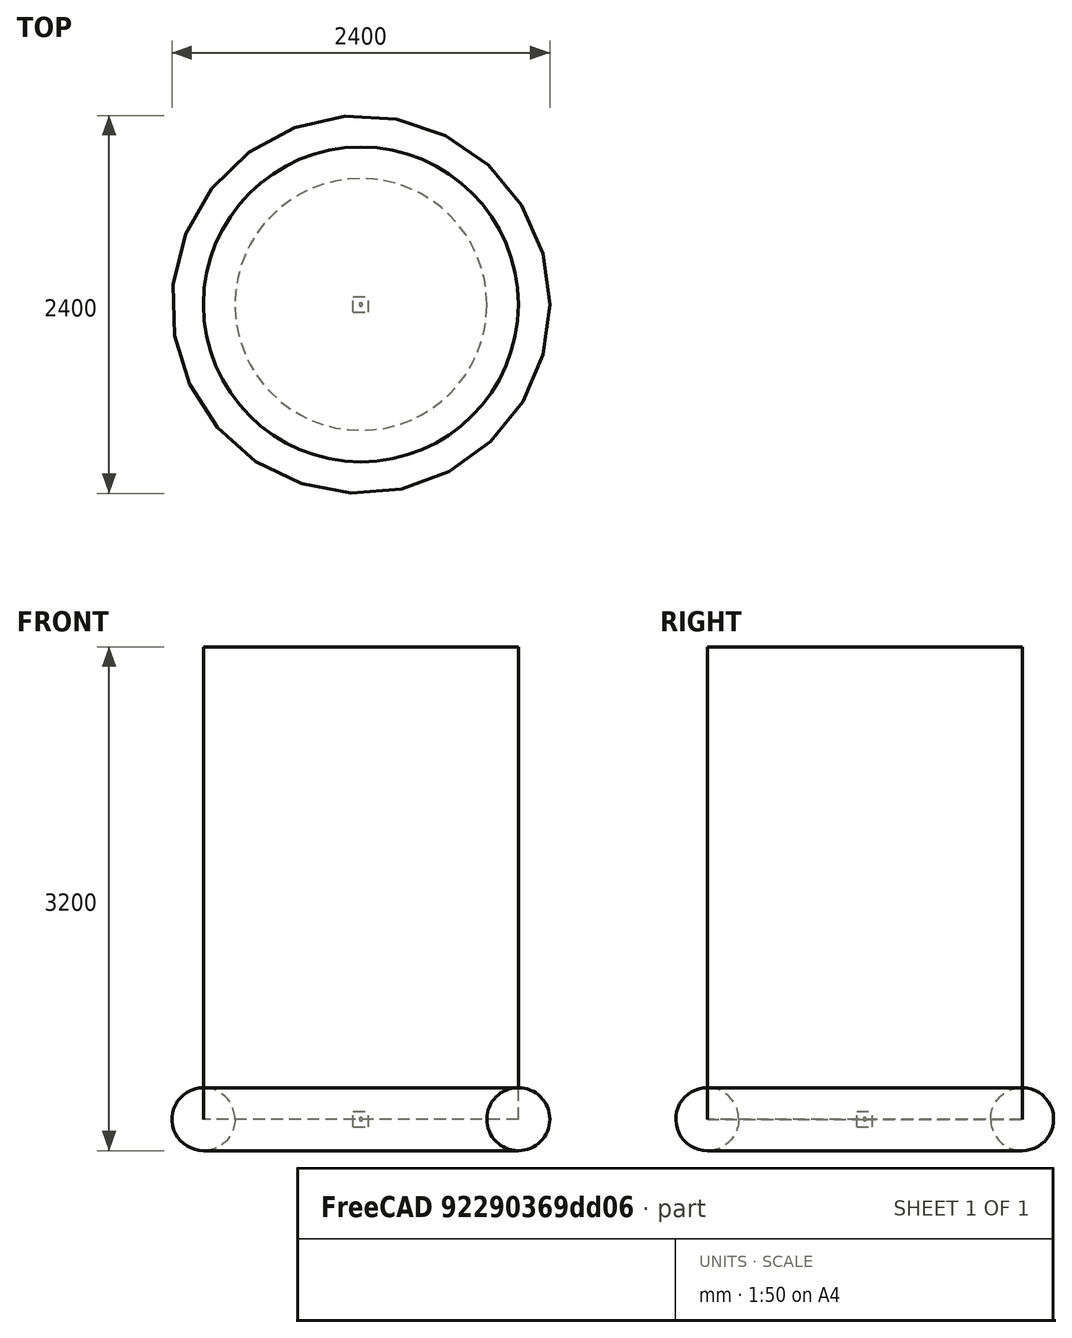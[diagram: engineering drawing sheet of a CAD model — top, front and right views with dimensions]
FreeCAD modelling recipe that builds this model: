
FCSTD DOCUMENT  (FreeCAD 0.20R)
Label: basicCAD
License: All rights reserved
LicenseURL: http://en.wikipedia.org/wiki/All_rights_reserved
objects: Mesh::Feature×6, Part::Torus×1, Part::Cylinder×1, Part::Sphere×1, Part::Plane×1, Part::Box×1
note: 5 computed .brp shape members not serialized (recipe doc carries the construction recipe); baked Part::Feature solids carry a one-line shape summary decoded from their .brp

FEATURE [Part::Torus] Torus
  Angle1 = -180
  Angle2 = 180
  Angle3 = 360
  AttacherType = Attacher::AttachEngine3D
  Radius1 = 1000
  Radius2 = 200
FEATURE [Mesh::Feature] Mesh  label="Torus (Meshed)"
FEATURE [Part::Cylinder] Cylinder
  Angle = 360
  AttacherType = Attacher::AttachEngine3D
  FirstAngle = 0
  Height = 3000
  Radius = 1000
  SecondAngle = 0
FEATURE [Mesh::Feature] Mesh001  label="Cylinder (Meshed)"
FEATURE [Part::Sphere] Sphere
  Angle1 = -90
  Angle2 = 90
  Angle3 = 360
  AttacherType = Attacher::AttachEngine3D
  Radius = 10
FEATURE [Mesh::Feature] Mesh002  label="Sphere (Meshed)"
FEATURE [Mesh::Feature] Mesh003  label="Sphere (Meshed)001"
FEATURE [Part::Plane] Plane
  AttacherType = Attacher::AttachEngine3D
  Length = 30
  Placement = pos=(-29,12.8978,-17.2235) rot=(0.707107,0,0.707107;3.14159rad)
  Width = 30
FEATURE [Mesh::Feature] Mesh004  label="Plane (Meshed)"
FEATURE [Part::Box] Box  label="Cube"
  AttacherType = Attacher::AttachEngine3D
  Height = 100
  Length = 100
  Placement = pos=(-50,-50,-50) rot=(0,0,1;0rad)
  Width = 100
FEATURE [Mesh::Feature] Mesh005  label="Cube (Meshed)"
  Placement = pos=(0,0,-1500) rot=(0,0,1;0rad)
